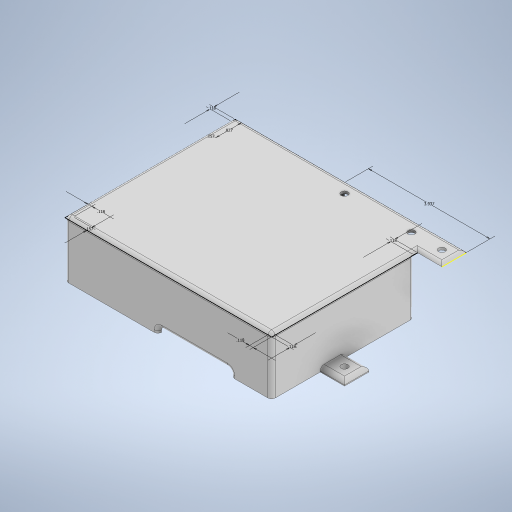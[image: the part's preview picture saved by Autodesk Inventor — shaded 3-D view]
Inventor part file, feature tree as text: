
AUTODESK INVENTOR PART (.ipt)
format: ipt  version: 2024.1 (Build 281209000, 209)  size: 349,184 bytes
history: native  units: in
note: dims shown in document units (in); Inventor stores cm internally (conversion verified against a paired STEP export)
features: sketch x6, extrude x5, hole x2, fillet x2
ambient origin geometry x8: Origin, YZ Plane, XZ Plane, XY Plane, X Axis, Y Axis, Z Axis, Center Point
bodies: Solid1 (feature_tree)
feature tree (15):
  extrude  "Extrusion1"  Depth=5.5118in
  sketch  "Sketch2"  dims[d2=0.0787in d3=0.0in d4=0.7874in]
  extrude  "Extrusion2"  Depth=0.7874in
  extrude  "Extrusion3"  Depth=3.937in
  extrude  "Extrusion4"  Depth=0.1181in
  hole  "Hole1"  [1 undecoded]
  extrude  "Extrusion5"  Depth=0.1575in
  hole  "Hole2"  [1 undecoded]
  fillet  "Fillet1"  Radius=0.8268in
  fillet  "Fillet2"  Radius=1.7717in
  sketch  "Sketch1"  dims[d0=6.6929in d1=5.5118in]
  sketch  "Sketch3"  dims[d5=0.7874in d6=3.937in]
  sketch  "Sketch5"  dims[d7=0.1181in d8=0.1181in]
  sketch  "Sketch6"  dims[d9=0.1181in d10=0.1181in]
  sketch  "Sketch7"  dims[d11=0.1181in d12=0.1575in d13=0.1575in d14=0.8268in d15=1.7717in d16=0.0in d17=0.5906in d18=0.0in d19=0.1969in d20=0.0in d21=0.125in d22=0.125in d23=0.3937in d24=0.3937in d25=1.378in d26=3.5433in d27=0.217in d28=0.5in d29=0.409in d30=0.25in d31=90.0deg d32=1.0in d33=0.8108in d34=3.5433in d35=0.7874in d36=0.7874in d37=0.0in d38=0.3937in d39=0.3937in d40=0.217in d41=0.75in d42=0.375in d43=0.25in d44=0.5635in d45=1.0in d46=0.8108in]
note: 2 required parameter values undecoded (feature->parameter linkage not recoverable at this tier; creation-order binding heuristic only, values carry confidence <= 0.55)
